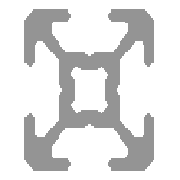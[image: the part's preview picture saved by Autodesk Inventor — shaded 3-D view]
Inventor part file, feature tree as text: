
AUTODESK INVENTOR PART (.ipt)
format: ipt  version: 2016 SP1 (Build 200210100, 210)  size: 385,536 bytes
history: native  units: mm
features: other x9, extrude x1, sketch x1
ambient origin geometry x8: Origin, YZ Plane, XZ Plane, XY Plane, X Axis, Y Axis, Z Axis, Center Point
bodies: Body1 (feature_tree)
feature tree (11):
  other  "20x20"
  other  "Table"
  other  "20x20-30"
  other  "20x20-360"
  other  "20x20-750"
  other  "20x20-500"
  other  "20x20-950"
  other  "Blocks"
  extrude  "Extrusion3"  [1 undecoded]
  sketch  "Sketch1"  dims[d23=0.0mm]
  other  "20x20:1"
note: 1 required parameter value undecoded (feature->parameter linkage not recoverable at this tier; creation-order binding heuristic only, values carry confidence <= 0.55)
